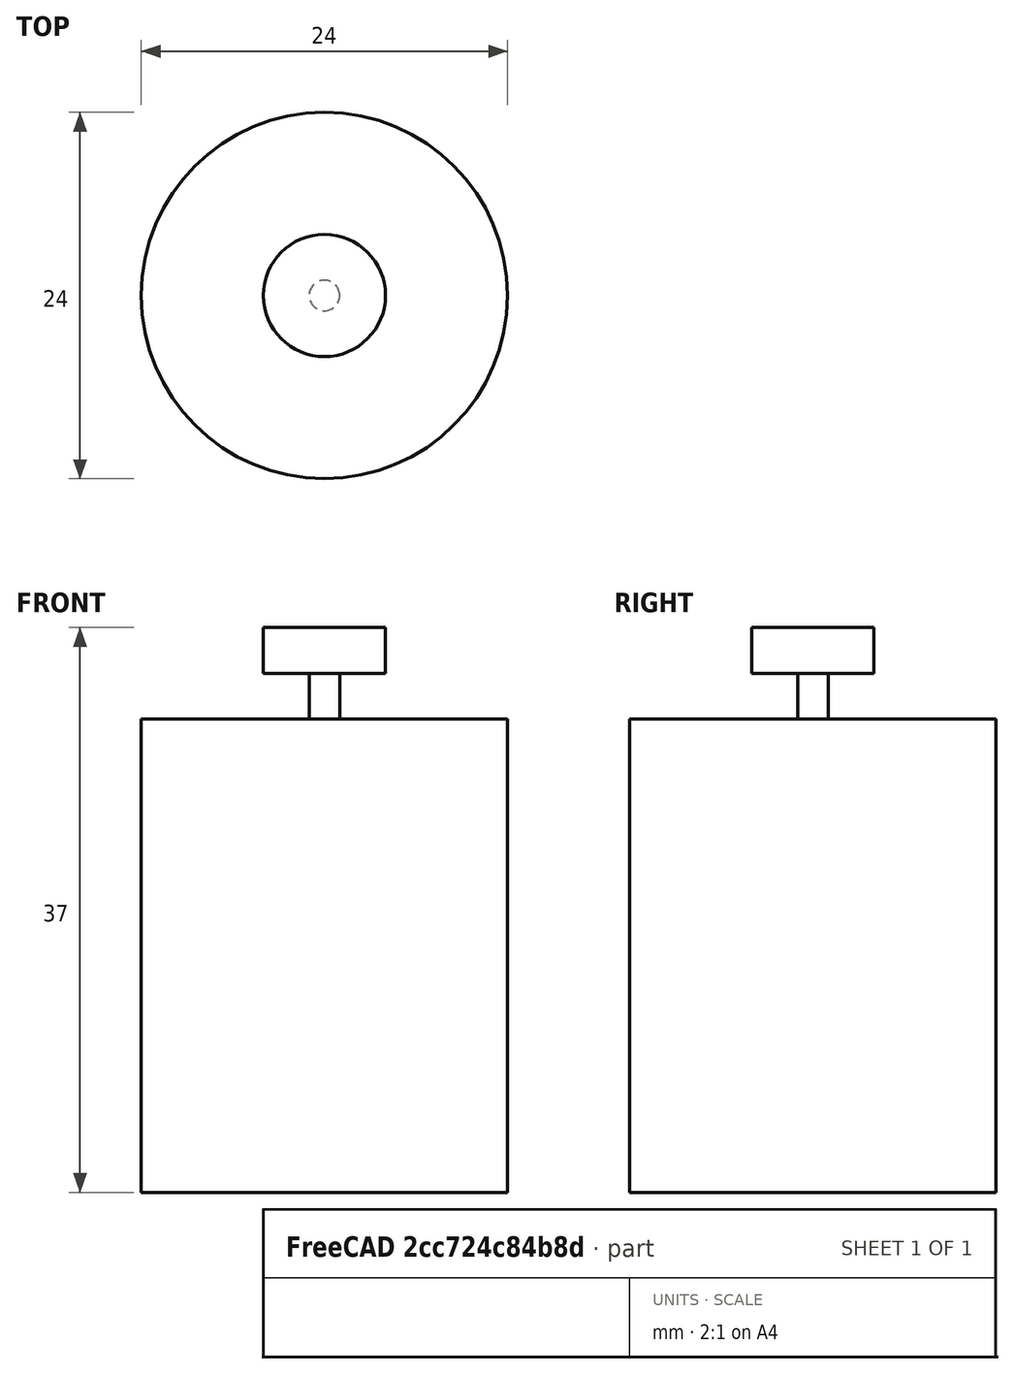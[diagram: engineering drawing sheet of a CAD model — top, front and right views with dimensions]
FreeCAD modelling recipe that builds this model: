
FCSTD DOCUMENT  (FreeCAD 0.14R3700 (Git))
Label: BR_Moteur
License: CC-BY 3.0
LicenseURL: http://creativecommons.org/licenses/by/3.0/
objects: Sketcher::SketchObject×1, Part::Revolution×1, Part::Feature×1
note: 3 computed .brp shape members not serialized (recipe doc carries the construction recipe); baked Part::Feature solids carry a one-line shape summary decoded from their .brp

FEATURE [Sketcher::SketchObject] Sketch
  Placement = pos=(0,0,0) rot=(1,0,0;1.5708rad)
  sketch-geometry (8):
    g0: LineSegment StartX=0 StartY=0 StartZ=0 EndX=12 EndY=0 EndZ=0
    g1: LineSegment StartX=12 StartY=0 StartZ=0 EndX=12 EndY=31 EndZ=0
    g2: LineSegment StartX=12 StartY=31 StartZ=0 EndX=1 EndY=31 EndZ=0
    g3: LineSegment StartX=0 StartY=0 StartZ=0 EndX=0 EndY=37 EndZ=0
    g4: LineSegment StartX=0 StartY=37 StartZ=0 EndX=4 EndY=37 EndZ=0
    g5: LineSegment StartX=4 StartY=37 StartZ=0 EndX=4 EndY=34 EndZ=0
    g6: LineSegment StartX=4 StartY=34 StartZ=0 EndX=1 EndY=34 EndZ=0
    g7: LineSegment StartX=1 StartY=34 StartZ=0 EndX=1 EndY=31 EndZ=0
  constraints (23):
    c: Coincident(g0,g-1)
    c: Horizontal(g0)
    c: Coincident(g1,g0)
    c: Vertical(g1)
    c: Horizontal(g2)
    c: Coincident(g3,g-1)
    c: PointOnObject(g3,g-2)
    c: Coincident(g4,g3)
    c: Horizontal(g4)
    c: Coincident(g5,g4)
    c: Coincident(g6,g5)
    c: Horizontal(g6)
    c: Coincident(g7,g6)
    c: Coincident(g7,g2)
    c: Vertical(g5)
    c: Vertical(g7)
    c: DistanceX(g6,g3) = -1
    c: DistanceY(g-1,g2) = 31
    c: DistanceX(g0) = 12
    c: DistanceX(g4) = 4
    c: DistanceY(g5) = -3
    c: DistanceY(g2,g3) = 6
    c: Coincident(g1,g2)
FEATURE [Part::Revolution] Revolve
  Angle = 360
  Axis = (0,0,1)
  Base = (0,0,0)
  Solid = true
  Source = -> Sketch
FEATURE [Part::Feature] Revolve001  label="Moteur"
  shape: bbox 24 x 24 x 37 mm, 7 faces (baked)
